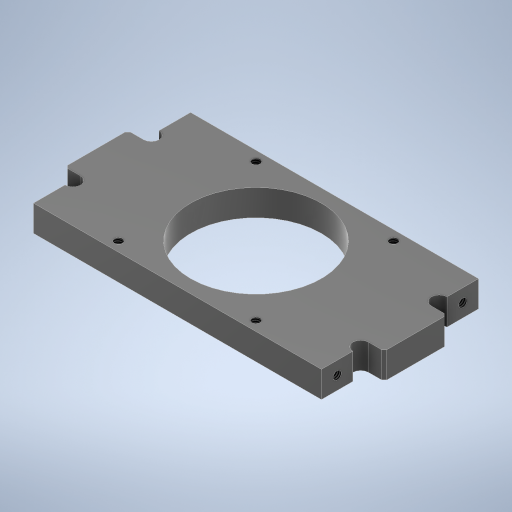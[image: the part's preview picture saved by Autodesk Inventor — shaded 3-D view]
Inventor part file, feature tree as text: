
AUTODESK INVENTOR PART (.ipt)
format: ipt  version: 2024.2 (Build 282272000, 272)  size: 348,160 bytes
history: native  units: mm
features: sketch x2, extrude x2, hole x1, mirror x1, chamfer x1
ambient origin geometry x8: Origin, YZ Plane, XZ Plane, XY Plane, X Axis, Y Axis, Z Axis, Center Point
bodies: Solid1 (feature_tree)
feature tree (7):
  sketch  "Sketch1"  dims[d0=26.28mm d1=26.28mm]
  extrude  "Extrusion1"  Depth=26.28mm
  extrude  "Extrusion2"  Depth=30.0mm
  hole  "Side-M2"  [1 undecoded]
  mirror  "Mirror1"
  chamfer  "C0.5"  Distance=3.0mm
  sketch  "Sketch2"  dims[d2=30.0mm d3=30.0mm d9=5.0mm d10=0.0mm d11=1.567mm d12=4.0mm d13=4.0mm d14=2.0mm d15=90.0deg d16=8.0mm d17=20.594885mm d19=3.0mm d20=12.0mm d31=0.0mm d32=0.0mm d37=55.0mm d40=6.0mm d41=6.0mm d42=1.567mm d43=4.0mm d44=4.0mm d45=2.0mm d46=90.0deg d47=6.0mm d48=0.0mm d50=12.5mm d54=0.5mm d55=2.0mm d56=45.0deg d57=30.0mm d60=1.5mm d62=25.0mm]
note: 1 required parameter value undecoded (feature->parameter linkage not recoverable at this tier; creation-order binding heuristic only, values carry confidence <= 0.55)
